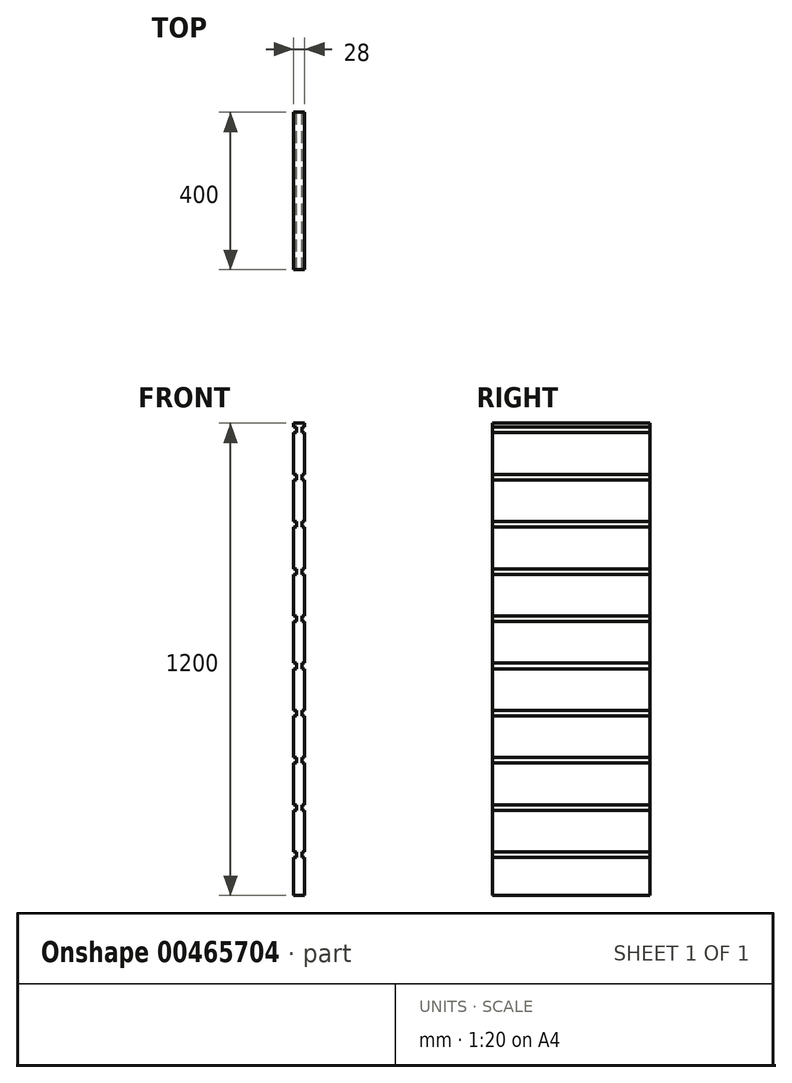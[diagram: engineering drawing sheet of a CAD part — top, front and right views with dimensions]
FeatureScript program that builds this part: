
annotation { "Feature Type Name" : "Feature", "Feature Type Description" : "" }
export const myFeature = defineFeature(function(context is Context, id is Id, definition is map)
    precondition{}
    {
        {
            var Q0;
            Q0=qCreatedBy(makeId("Front.planeOp"),FACE);
            var sketch = newSketch(context, id + "F0", { "sketchPlane" : qUnion([Q0])});
            skLineSegment(sketch, "E0", {"start": v(0, 0) * mm, "end": v(14, 0) * mm});
            skLineSegment(sketch, "E1", {"start": v(14, 0) * mm, "end": v(14, 96) * mm});
            skLineSegment(sketch, "E2", {"start": v(14, 1176) * mm, "end": v(7, 1176) * mm});
            skLineSegment(sketch, "E3", {"start": v(7, 1176) * mm, "end": v(7, 1190) * mm});
            skLineSegment(sketch, "E4", {"start": v(7, 1190) * mm, "end": v(14, 1190) * mm});
            skLineSegment(sketch, "E5", {"start": v(14, 1190) * mm, "end": v(14, 1200) * mm});
            skLineSegment(sketch, "E6", {"start": v(14, 1200) * mm, "end": v(0, 1200) * mm});
            skLineSegment(sketch, "E7", {"start": v(0, 1200) * mm, "end": v(0, 0) * mm, "construction": true});
            skLineSegment(sketch, "E8.0.1.0", {"start": v(14, 1056) * mm, "end": v(7, 1056) * mm});
            skLineSegment(sketch, "E8.0.1.1", {"start": v(7, 1056) * mm, "end": v(7, 1070) * mm});
            skLineSegment(sketch, "E8.0.1.2", {"start": v(7, 1070) * mm, "end": v(14, 1070) * mm});
            skLineSegment(sketch, "E8.0.2.0", {"start": v(14, 936) * mm, "end": v(7, 936) * mm});
            skLineSegment(sketch, "E8.0.2.1", {"start": v(7, 936) * mm, "end": v(7, 950) * mm});
            skLineSegment(sketch, "E8.0.2.2", {"start": v(7, 950) * mm, "end": v(14, 950) * mm});
            skLineSegment(sketch, "E8.0.3.0", {"start": v(14, 816) * mm, "end": v(7, 816) * mm});
            skLineSegment(sketch, "E8.0.3.1", {"start": v(7, 816) * mm, "end": v(7, 830) * mm});
            skLineSegment(sketch, "E8.0.3.2", {"start": v(7, 830) * mm, "end": v(14, 830) * mm});
            skLineSegment(sketch, "E8.0.4.0", {"start": v(14, 696) * mm, "end": v(7, 696) * mm});
            skLineSegment(sketch, "E8.0.4.1", {"start": v(7, 696) * mm, "end": v(7, 710) * mm});
            skLineSegment(sketch, "E8.0.4.2", {"start": v(7, 710) * mm, "end": v(14, 710) * mm});
            skLineSegment(sketch, "E8.0.5.0", {"start": v(14, 576) * mm, "end": v(7, 576) * mm});
            skLineSegment(sketch, "E8.0.5.1", {"start": v(7, 576) * mm, "end": v(7, 590) * mm});
            skLineSegment(sketch, "E8.0.5.2", {"start": v(7, 590) * mm, "end": v(14, 590) * mm});
            skLineSegment(sketch, "E8.0.6.0", {"start": v(14, 456) * mm, "end": v(7, 456) * mm});
            skLineSegment(sketch, "E8.0.6.1", {"start": v(7, 456) * mm, "end": v(7, 470) * mm});
            skLineSegment(sketch, "E8.0.6.2", {"start": v(7, 470) * mm, "end": v(14, 470) * mm});
            skLineSegment(sketch, "E8.0.7.0", {"start": v(14, 336) * mm, "end": v(7, 336) * mm});
            skLineSegment(sketch, "E8.0.7.1", {"start": v(7, 336) * mm, "end": v(7, 350) * mm});
            skLineSegment(sketch, "E8.0.7.2", {"start": v(7, 350) * mm, "end": v(14, 350) * mm});
            skLineSegment(sketch, "E8.0.8.0", {"start": v(14, 216) * mm, "end": v(7, 216) * mm});
            skLineSegment(sketch, "E8.0.8.1", {"start": v(7, 216) * mm, "end": v(7, 230) * mm});
            skLineSegment(sketch, "E8.0.8.2", {"start": v(7, 230) * mm, "end": v(14, 230) * mm});
            skLineSegment(sketch, "E8.0.9.0", {"start": v(14, 96) * mm, "end": v(7, 96) * mm});
            skLineSegment(sketch, "E8.0.9.1", {"start": v(7, 96) * mm, "end": v(7, 110) * mm});
            skLineSegment(sketch, "E8.0.9.2", {"start": v(7, 110) * mm, "end": v(14, 110) * mm});
            skLineSegment(sketch, "E8.direction1", {"start": v(7, 1176) * mm, "end": v(85.77, 1176) * mm, "construction": true});
            skLineSegment(sketch, "E8.direction2", {"start": v(7, 1176) * mm, "end": v(7, 1056) * mm, "construction": true});
            skLineSegment(sketch, "E9.trimOffspring", {"start": v(14, 1070) * mm, "end": v(14, 1176) * mm});
            skLineSegment(sketch, "E10.trimOffspring", {"start": v(14, 950) * mm, "end": v(14, 1056) * mm});
            skLineSegment(sketch, "E11.trimOffspring", {"start": v(14, 830) * mm, "end": v(14, 936) * mm});
            skLineSegment(sketch, "E12.trimOffspring", {"start": v(14, 710) * mm, "end": v(14, 816) * mm});
            skLineSegment(sketch, "E13.trimOffspring", {"start": v(14, 590) * mm, "end": v(14, 696) * mm});
            skLineSegment(sketch, "E14.trimOffspring", {"start": v(14, 470) * mm, "end": v(14, 576) * mm});
            skLineSegment(sketch, "E15.trimOffspring", {"start": v(14, 350) * mm, "end": v(14, 456) * mm});
            skLineSegment(sketch, "E16.trimOffspring", {"start": v(14, 230) * mm, "end": v(14, 336) * mm});
            skLineSegment(sketch, "E17.trimOffspring", {"start": v(14, 110) * mm, "end": v(14, 216) * mm});
            skLineSegment(sketch, "E18.MirrorCS", {"start": v(-7, 1190) * mm, "end": v(-14, 1190) * mm});
            skLineSegment(sketch, "E19.MirrorCS", {"start": v(-7, 1176) * mm, "end": v(-7, 1056) * mm, "construction": true});
            skLineSegment(sketch, "E20.MirrorCS", {"start": v(-7, 1176) * mm, "end": v(-85.77, 1176) * mm, "construction": true});
            skLineSegment(sketch, "E21.MirrorCS", {"start": v(-14, 1176) * mm, "end": v(-7, 1176) * mm});
            skLineSegment(sketch, "E22.MirrorCS", {"start": v(-7, 1176) * mm, "end": v(-7, 1190) * mm});
            skLineSegment(sketch, "E23.MirrorCS", {"start": v(-14, 1190) * mm, "end": v(-14, 1200) * mm});
            skLineSegment(sketch, "E24.MirrorCS", {"start": v(-14, 1056) * mm, "end": v(-7, 1056) * mm});
            skLineSegment(sketch, "E25.MirrorCS", {"start": v(-7, 1056) * mm, "end": v(-7, 1070) * mm});
            skLineSegment(sketch, "E26.MirrorCS", {"start": v(-7, 1070) * mm, "end": v(-14, 1070) * mm});
            skLineSegment(sketch, "E27.MirrorCS", {"start": v(-7, 336) * mm, "end": v(-7, 350) * mm});
            skLineSegment(sketch, "E28.MirrorCS", {"start": v(-7, 470) * mm, "end": v(-14, 470) * mm});
            skLineSegment(sketch, "E29.MirrorCS", {"start": v(-14, 456) * mm, "end": v(-7, 456) * mm});
            skLineSegment(sketch, "E30.MirrorCS", {"start": v(-14, 576) * mm, "end": v(-7, 576) * mm});
            skLineSegment(sketch, "E31.MirrorCS", {"start": v(-7, 230) * mm, "end": v(-14, 230) * mm});
            skLineSegment(sketch, "E32.MirrorCS", {"start": v(-14, 216) * mm, "end": v(-7, 216) * mm});
            skLineSegment(sketch, "E33.MirrorCS", {"start": v(-7, 110) * mm, "end": v(-14, 110) * mm});
            skLineSegment(sketch, "E34.MirrorCS", {"start": v(-7, 830) * mm, "end": v(-14, 830) * mm});
            skLineSegment(sketch, "E35.MirrorCS", {"start": v(-7, 696) * mm, "end": v(-7, 710) * mm});
            skLineSegment(sketch, "E36.MirrorCS", {"start": v(-14, 96) * mm, "end": v(-7, 96) * mm});
            skLineSegment(sketch, "E37.MirrorCS", {"start": v(-7, 936) * mm, "end": v(-7, 950) * mm});
            skLineSegment(sketch, "E38.MirrorCS", {"start": v(-14, 936) * mm, "end": v(-7, 936) * mm});
            skLineSegment(sketch, "E39.MirrorCS", {"start": v(-7, 350) * mm, "end": v(-14, 350) * mm});
            skLineSegment(sketch, "E40.MirrorCS", {"start": v(-7, 456) * mm, "end": v(-7, 470) * mm});
            skLineSegment(sketch, "E41.MirrorCS", {"start": v(-7, 576) * mm, "end": v(-7, 590) * mm});
            skLineSegment(sketch, "E42.MirrorCS", {"start": v(-7, 216) * mm, "end": v(-7, 230) * mm});
            skLineSegment(sketch, "E43.MirrorCS", {"start": v(-7, 710) * mm, "end": v(-14, 710) * mm});
            skLineSegment(sketch, "E44.MirrorCS", {"start": v(-14, 696) * mm, "end": v(-7, 696) * mm});
            skLineSegment(sketch, "E45.MirrorCS", {"start": v(-7, 950) * mm, "end": v(-14, 950) * mm});
            skLineSegment(sketch, "E46.MirrorCS", {"start": v(-14, 816) * mm, "end": v(-7, 816) * mm});
            skLineSegment(sketch, "E47.MirrorCS", {"start": v(-7, 816) * mm, "end": v(-7, 830) * mm});
            skLineSegment(sketch, "E48.MirrorCS", {"start": v(-7, 96) * mm, "end": v(-7, 110) * mm});
            skLineSegment(sketch, "E49.MirrorCS", {"start": v(-14, 336) * mm, "end": v(-7, 336) * mm});
            skLineSegment(sketch, "E50.MirrorCS", {"start": v(-7, 590) * mm, "end": v(-14, 590) * mm});
            skLineSegment(sketch, "E51.MirrorCS", {"start": v(-14, 830) * mm, "end": v(-14, 936) * mm});
            skLineSegment(sketch, "E52.MirrorCS", {"start": v(-14, 110) * mm, "end": v(-14, 216) * mm});
            skLineSegment(sketch, "E53.MirrorCS", {"start": v(-14, 710) * mm, "end": v(-14, 816) * mm});
            skLineSegment(sketch, "E54.MirrorCS", {"start": v(-14, 230) * mm, "end": v(-14, 336) * mm});
            skLineSegment(sketch, "E55.MirrorCS", {"start": v(-14, 470) * mm, "end": v(-14, 576) * mm});
            skLineSegment(sketch, "E56.MirrorCS", {"start": v(-14, 1070) * mm, "end": v(-14, 1176) * mm});
            skLineSegment(sketch, "E57.MirrorCS", {"start": v(0, 0) * mm, "end": v(-14, 0) * mm});
            skLineSegment(sketch, "E58.MirrorCS", {"start": v(-14, 0) * mm, "end": v(-14, 96) * mm});
            skLineSegment(sketch, "E59.MirrorCS", {"start": v(-14, 1200) * mm, "end": v(0, 1200) * mm});
            skLineSegment(sketch, "E60.MirrorCS", {"start": v(-14, 590) * mm, "end": v(-14, 696) * mm});
            skLineSegment(sketch, "E61.MirrorCS", {"start": v(-14, 950) * mm, "end": v(-14, 1056) * mm});
            skLineSegment(sketch, "E62.MirrorCS", {"start": v(-14, 350) * mm, "end": v(-14, 456) * mm});
            skSolve(sketch);
        }
        {
            var Q0;
            Q0 = qSketchRegion(id + "F0", true);
            extrude(context, id + "F1", {"entities" : qUnion([Q0]), "depth" : 400 * mm});
        }
    });
